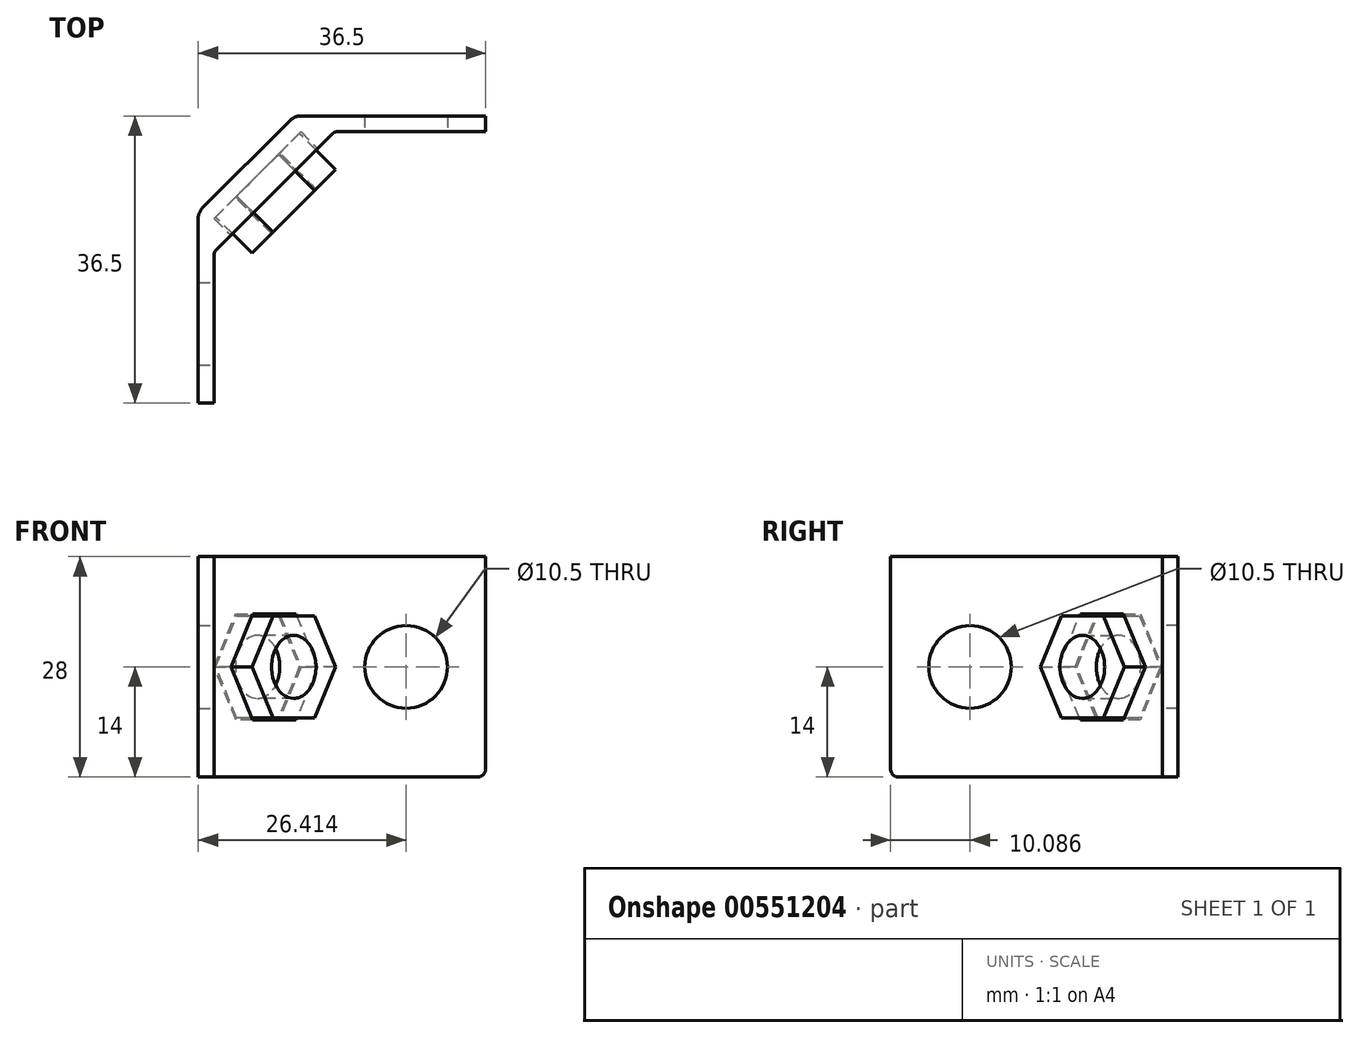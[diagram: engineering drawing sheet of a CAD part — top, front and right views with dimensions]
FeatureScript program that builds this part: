
annotation { "Feature Type Name" : "Feature", "Feature Type Description" : "" }
export const myFeature = defineFeature(function(context is Context, id is Id, definition is map)
    precondition{}
    {
        {
            var Q0;
            Q0=qCreatedBy(makeId("Top.planeOp"),FACE);
            var sketch = newSketch(context, id + "F0", { "sketchPlane" : qUnion([Q0])});
            skLineSegment(sketch, "E0.bottom", {"start": v(-19.75, 19.75) * mm, "end": v(19.75, 19.75) * mm, "construction": true});
            skLineSegment(sketch, "E0.top", {"start": v(-19.75, -19.75) * mm, "end": v(19.75, -19.75) * mm, "construction": true});
            skLineSegment(sketch, "E0.left", {"start": v(-19.75, 19.75) * mm, "end": v(-19.75, -19.75) * mm, "construction": true});
            skLineSegment(sketch, "E0.right", {"start": v(19.75, 19.75) * mm, "end": v(19.75, -19.75) * mm, "construction": true});
            skLineSegment(sketch, "E1", {"start": v(-19.75, -19.75) * mm, "end": v(-19.75, 3.25) * mm});
            skLineSegment(sketch, "E2", {"start": v(19.75, 19.75) * mm, "end": v(-3.25, 19.75) * mm});
            skLineSegment(sketch, "E3", {"start": v(-19.75, 3.25) * mm, "end": v(-3.25, 19.75) * mm, "construction": true});
            skLineSegment(sketch, "E4", {"start": v(-19.75, -19.75) * mm, "end": v(-17.75, -19.75) * mm});
            skLineSegment(sketch, "E5.0", {"start": v(19.75, 17.75) * mm, "end": v(-2.42, 17.75) * mm});
            skLineSegment(sketch, "E5.1", {"start": v(-17.75, 2.42) * mm, "end": v(-2.42, 17.75) * mm});
            skLineSegment(sketch, "E5.2", {"start": v(-17.75, -19.75) * mm, "end": v(-17.75, 2.42) * mm});
            skLineSegment(sketch, "E6", {"start": v(19.75, 17.75) * mm, "end": v(19.75, 19.75) * mm});
            skLineSegment(sketch, "E7.0", {"start": v(-19.75, 7.5) * mm, "end": v(-7.5, 19.75) * mm});
            skLineSegment(sketch, "E8", {"start": v(-3.25, 19.75) * mm, "end": v(-7.5, 19.75) * mm});
            skLineSegment(sketch, "E9", {"start": v(-19.75, 3.25) * mm, "end": v(-19.75, 7.5) * mm});
            skSolve(sketch);
        }
        {
            var Q0;
            Q0 = qSketchRegion(id + "F0", true);
            extrude(context, id + "F1", {"entities" : qUnion([Q0]), "depth" : 28 * mm, "offsetDistance" : 25 * mm});
        }
        {
            var Q0;
            Q0=makeQuery(id+"F1.opExtrude","SWEPT_FACE",FACE,{"disambiguationData":[OSD([sQuery(id+"F0.wireOp",EDGE,"E5.2")])]});
            var sketch = newSketch(context, id + "F2", { "sketchPlane" : qUnion([Q0])});
            skLineSegment(sketch, "E10", {"start": v(-8.66, 28) * mm, "end": v(-8.66, 0) * mm, "construction": true});
            skCircle(sketch, "E11", {"center": v(-6.66, 14) * mm, "radius": 5.25 * mm});
            skSolve(sketch);
        }
        {
            var Q0;
            Q0=makeQuery(id+"F1.opExtrude","SWEPT_FACE",FACE,{"disambiguationData":[OSD([sQuery(id+"F0.wireOp",EDGE,"E5.0")])]});
            var sketch = newSketch(context, id + "F3", { "sketchPlane" : qUnion([Q0])});
            skLineSegment(sketch, "E12", {"start": v(8.66, 28) * mm, "end": v(8.66, 0) * mm, "construction": true});
            skCircle(sketch, "E13", {"center": v(6.66, 14) * mm, "radius": 5.25 * mm});
            skSolve(sketch);
        }
        {
            var Q0;
            Q0 = qSketchRegion(id + "F3", true);
            extrude(context, id + "F4", {"entities" : qUnion([Q0]), "operationType" : NewBodyOperationType.REMOVE, "oppositeDirection" : true, "depth" : 25 * mm, "offsetDistance" : 25 * mm});
        }
        {
            var Q0;
            Q0=makeQuery(id+"F1.opExtrude","SWEPT_FACE",FACE,{"disambiguationData":[OSD([sQuery(id+"F0.wireOp",EDGE,"E5.1")])]});
            var sketch = newSketch(context, id + "F5", { "sketchPlane" : qUnion([Q0])});
            skLineSegment(sketch, "E14", {"start": v(0, 28) * mm, "end": v(0, 0) * mm, "construction": true});
            skCircle(sketch, "E15.cCircle", {"center": v(0, 14) * mm, "radius": 6.75 * mm, "construction": true});
            skLineSegment(sketch, "E15.0", {"start": v(3.9, 7.25) * mm, "end": v(-3.9, 7.25) * mm});
            skLineSegment(sketch, "E15.1", {"start": v(-3.9, 7.25) * mm, "end": v(-7.8, 14) * mm});
            skLineSegment(sketch, "E15.2", {"start": v(-7.8, 14) * mm, "end": v(-3.9, 20.75) * mm});
            skLineSegment(sketch, "E15.3", {"start": v(-3.9, 20.75) * mm, "end": v(3.9, 20.75) * mm});
            skLineSegment(sketch, "E15.4", {"start": v(3.9, 20.75) * mm, "end": v(7.8, 14) * mm});
            skLineSegment(sketch, "E15.5", {"start": v(7.8, 14) * mm, "end": v(3.9, 7.25) * mm});
            skPoint(sketch, "E15.0.midPoint", {"position": v(0, 7.25) * mm});
            skSolve(sketch);
        }
        {
            var Q0;
            Q0 = qSketchRegion(id + "F5", true);
            extrude(context, id + "F6", {"entities" : qUnion([Q0]), "operationType" : NewBodyOperationType.REMOVE, "oppositeDirection" : true, "depth" : 3 * mm, "offsetDistance" : 25 * mm});
        }
        {
            var Q0;
            Q0=makeQuery(id+"F6.boolean.opBoolean","COPY",FACE,{"derivedFrom":makeQuery(id+"F6.opExtrude","CAP_FACE",FACE,{"disambiguationData":[OSD([sQuery(id+"F5.wireOp",EDGE,"E15.0"),sQuery(id+"F5.wireOp",EDGE,"E15.1"),sQuery(id+"F5.wireOp",EDGE,"E15.2"),sQuery(id+"F5.wireOp",EDGE,"E15.3"),sQuery(id+"F5.wireOp",EDGE,"E15.4"),sQuery(id+"F5.wireOp",EDGE,"E15.5")])],"isStart":false})});
            var sketch = newSketch(context, id + "F7", { "sketchPlane" : qUnion([Q0])});
            skLineSegment(sketch, "E16", {"start": v(0, 20.75) * mm, "end": v(0, 7.25) * mm, "construction": true});
            skCircle(sketch, "E17.cCircle", {"center": v(0, 14) * mm, "radius": 6.5 * mm, "construction": true});
            skLineSegment(sketch, "E17.0", {"start": v(-3.75, 20.5) * mm, "end": v(3.75, 20.5) * mm});
            skLineSegment(sketch, "E17.1", {"start": v(3.75, 20.5) * mm, "end": v(7.5, 14) * mm});
            skLineSegment(sketch, "E17.2", {"start": v(7.5, 14) * mm, "end": v(3.75, 7.5) * mm});
            skLineSegment(sketch, "E17.3", {"start": v(3.75, 7.5) * mm, "end": v(-3.75, 7.5) * mm});
            skLineSegment(sketch, "E17.4", {"start": v(-3.75, 7.5) * mm, "end": v(-7.5, 14) * mm});
            skLineSegment(sketch, "E17.5", {"start": v(-7.5, 14) * mm, "end": v(-3.75, 20.5) * mm});
            skPoint(sketch, "E17.0.midPoint", {"position": v(0, 20.5) * mm});
            skCircle(sketch, "E18", {"center": v(0, 14) * mm, "radius": 4 * mm});
            skSolve(sketch);
        }
        {
            var Q0;
            Q0 = qSketchRegion(id + "F7", true);
            extrude(context, id + "F8", {"entities" : qUnion([Q0]), "operationType" : NewBodyOperationType.ADD, "depth" : 6.5 * mm, "offsetDistance" : 25 * mm});
        }
        {
            var Q0;
            Q0=makeQuery(id+"F1.opExtrude","CAP_FACE",FACE,{"disambiguationData":[OSD([sQuery(id+"F0.wireOp",EDGE,"E1"),sQuery(id+"F0.wireOp",EDGE,"E2"),sQuery(id+"F0.wireOp",EDGE,"E4"),sQuery(id+"F0.wireOp",EDGE,"E5.0"),sQuery(id+"F0.wireOp",EDGE,"E5.1"),sQuery(id+"F0.wireOp",EDGE,"E5.2"),sQuery(id+"F0.wireOp",EDGE,"E6"),sQuery(id+"F0.wireOp",EDGE,"E7.0"),sQuery(id+"F0.wireOp",EDGE,"E8"),sQuery(id+"F0.wireOp",EDGE,"E9")])],"isStart":false});
            var sketch = newSketch(context, id + "F9", { "sketchPlane" : qUnion([Q0])});
            skLineSegment(sketch, "E19.bottom", {"start": v(-19.75, -19.75) * mm, "end": v(-17.75, -19.75) * mm});
            skLineSegment(sketch, "E19.top", {"start": v(-19.75, -16.75) * mm, "end": v(-17.75, -16.75) * mm});
            skLineSegment(sketch, "E19.left", {"start": v(-19.75, -19.75) * mm, "end": v(-19.75, -16.75) * mm});
            skLineSegment(sketch, "E19.right", {"start": v(-17.75, -19.75) * mm, "end": v(-17.75, -16.75) * mm});
            skLineSegment(sketch, "E20.bottom", {"start": v(19.75, 17.75) * mm, "end": v(16.75, 17.75) * mm});
            skLineSegment(sketch, "E20.top", {"start": v(19.75, 19.75) * mm, "end": v(16.75, 19.75) * mm});
            skLineSegment(sketch, "E20.left", {"start": v(19.75, 17.75) * mm, "end": v(19.75, 19.75) * mm});
            skLineSegment(sketch, "E20.right", {"start": v(16.75, 17.75) * mm, "end": v(16.75, 19.75) * mm});
            skSolve(sketch);
        }
        {
            var Q0;
            Q0 = qSketchRegion(id + "F9", true);
            extrude(context, id + "F10", {"entities" : qUnion([Q0]), "operationType" : NewBodyOperationType.REMOVE, "endBound" : BoundingType.THROUGH_ALL, "oppositeDirection" : true, "depth" : 25 * mm, "offsetDistance" : 25 * mm});
        }
        {
            var Q0;
            Q0 = qSketchRegion(id + "F2", true);
            extrude(context, id + "F11", {"entities" : qUnion([Q0]), "operationType" : NewBodyOperationType.REMOVE, "oppositeDirection" : true, "depth" : 25 * mm, "offsetDistance" : 25 * mm});
        }
        {
            var Q0;
            Q0=makeQuery(id+"F1.opExtrude","SWEPT_EDGE",EDGE,{"disambiguationData":[OSD([sQuery(id+"F0.wireOp",EDGE,"E5.1"),sQuery(id+"F0.wireOp",EDGE,"E5.2")])]});
            var Q1;
            Q1=makeQuery(id+"F1.opExtrude","SWEPT_EDGE",EDGE,{"disambiguationData":[OSD([sQuery(id+"F0.wireOp",EDGE,"E5.0"),sQuery(id+"F0.wireOp",EDGE,"E5.1")])]});
            var Q2;
            Q2=makeQuery(id+"F10.boolean.opBoolean","COPY",EDGE,{"derivedFrom":makeQuery(id+"F10.opExtrude","CAP_EDGE",EDGE,{"disambiguationData":[OSD([sQuery(id+"F9.wireOp",EDGE,"E20.right")])],"isStart":true})});
            var Q3;
            Q3=makeQuery(id+"F10.boolean.opBoolean","INTERSECT",EDGE,{"derivedFrom":[makeQuery(id+"F1.opExtrude","CAP_FACE",FACE,{"disambiguationData":[OSD([sQuery(id+"F0.wireOp",EDGE,"E1"),sQuery(id+"F0.wireOp",EDGE,"E2"),sQuery(id+"F0.wireOp",EDGE,"E4"),sQuery(id+"F0.wireOp",EDGE,"E5.0"),sQuery(id+"F0.wireOp",EDGE,"E5.1"),sQuery(id+"F0.wireOp",EDGE,"E5.2"),sQuery(id+"F0.wireOp",EDGE,"E6"),sQuery(id+"F0.wireOp",EDGE,"E7.0"),sQuery(id+"F0.wireOp",EDGE,"E8"),sQuery(id+"F0.wireOp",EDGE,"E9")])],"isStart":true}),makeQuery(id+"F10.opExtrude","SWEPT_FACE",FACE,{"disambiguationData":[OSD([sQuery(id+"F9.wireOp",EDGE,"E20.right")])]})]});
            var Q4;
            Q4=makeQuery(id+"F10.boolean.opBoolean","COPY",EDGE,{"derivedFrom":makeQuery(id+"F10.opExtrude","CAP_EDGE",EDGE,{"disambiguationData":[OSD([sQuery(id+"F9.wireOp",EDGE,"E19.top")])],"isStart":true})});
            var Q5;
            Q5=makeQuery(id+"F10.boolean.opBoolean","INTERSECT",EDGE,{"derivedFrom":[makeQuery(id+"F1.opExtrude","CAP_FACE",FACE,{"disambiguationData":[OSD([sQuery(id+"F0.wireOp",EDGE,"E1"),sQuery(id+"F0.wireOp",EDGE,"E2"),sQuery(id+"F0.wireOp",EDGE,"E4"),sQuery(id+"F0.wireOp",EDGE,"E5.0"),sQuery(id+"F0.wireOp",EDGE,"E5.1"),sQuery(id+"F0.wireOp",EDGE,"E5.2"),sQuery(id+"F0.wireOp",EDGE,"E6"),sQuery(id+"F0.wireOp",EDGE,"E7.0"),sQuery(id+"F0.wireOp",EDGE,"E8"),sQuery(id+"F0.wireOp",EDGE,"E9")])],"isStart":true}),makeQuery(id+"F10.opExtrude","SWEPT_FACE",FACE,{"disambiguationData":[OSD([sQuery(id+"F9.wireOp",EDGE,"E19.top")])]})]});
            fillet(context, id + "F12", {"entities" : qUnion([Q0, Q1, Q2, Q3, Q4, Q5]), "radius" : 1 * mm, "tangentPropagation" : true, "allowEdgeOverflow" : false});
        }
        {
            var Q0;
            Q0=makeQuery(id+"F1.opExtrude","SWEPT_EDGE",EDGE,{"disambiguationData":[OSD([sQuery(id+"F0.wireOp",EDGE,"E7.0"),sQuery(id+"F0.wireOp",EDGE,"E9")])]});
            var Q1;
            Q1=makeQuery(id+"F1.opExtrude","SWEPT_EDGE",EDGE,{"disambiguationData":[OSD([sQuery(id+"F0.wireOp",EDGE,"E7.0"),sQuery(id+"F0.wireOp",EDGE,"E8")])]});
            fillet(context, id + "F13", {"entities" : qUnion([Q0, Q1]), "radius" : 2 * mm, "tangentPropagation" : true, "allowEdgeOverflow" : false});
        }
    });
